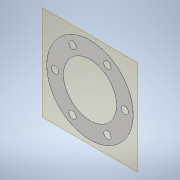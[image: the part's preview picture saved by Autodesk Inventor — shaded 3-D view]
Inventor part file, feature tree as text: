
AUTODESK INVENTOR PART (.ipt)
format: ipt  version: 2020 (Build 240168000, 168)  size: 116,736 bytes
history: native  units: mm
features: other x3, plane x1, extrude x1, sketch x1, reference x1
ambient origin geometry x8: Origin, YZ Plane, XZ Plane, XY Plane, X Axis, Y Axis, Z Axis, Center Point
bodies: 实体1 (feature_tree)
feature tree (7):
  plane  "工作平面1"
  extrude  "拉伸1"  [1 undecoded]
  sketch  "草图1"  dims[d0=0.15mm d1=0.0mm]
  reference  "参考1"
  other  "<userpath>\Desktop\ME_course_project\课设试试\shaft_try_1.iam"
  other  "shaft_try_1.iam"
  other  "轴承端盖1:1"
note: 1 required parameter value undecoded (feature->parameter linkage not recoverable at this tier; creation-order binding heuristic only, values carry confidence <= 0.55)
